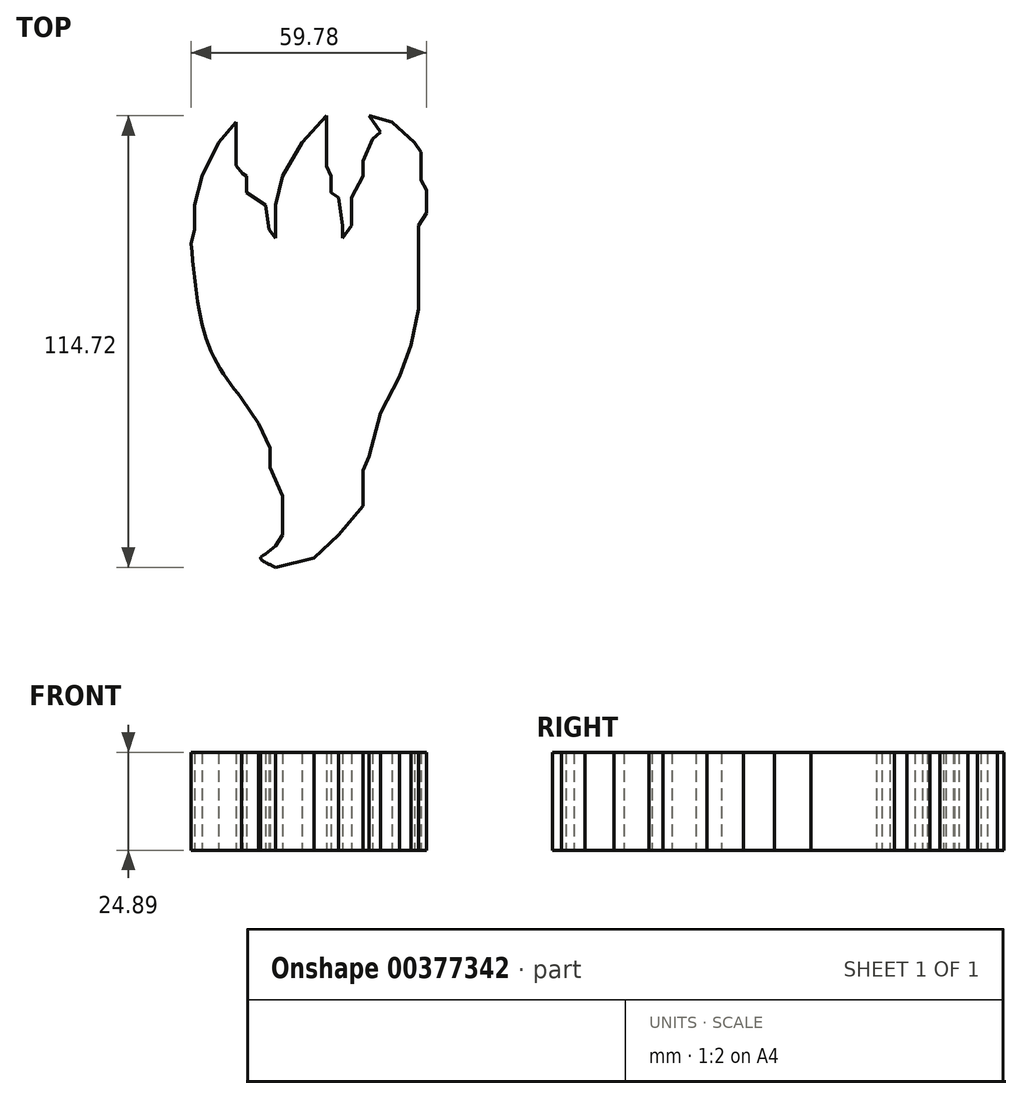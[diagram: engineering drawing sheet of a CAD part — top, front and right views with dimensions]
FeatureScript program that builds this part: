
annotation { "Feature Type Name" : "Feature", "Feature Type Description" : "" }
export const myFeature = defineFeature(function(context is Context, id is Id, definition is map)
    precondition{}
    {
        {
            var Q0;
            Q0=qCreatedBy(makeId("Top.planeOp"),FACE);
            var sketch = newSketch(context, id + "F0", { "sketchPlane" : qUnion([Q0])});
            skFitSpline(sketch, "E0", {"points": [v(-31.15, 30.49) * mm, v(-26.9, 4.93) * mm, v(-18.37, -8.92) * mm], "startDerivative": vector(4.39, -49.85) * mm, "endDerivative": vector(21.85, -28.13) * mm});
            skFitSpline(sketch, "E1", {"points": [v(-14.11, -15.3) * mm, v(-11.18, -21.43) * mm], "startDerivative": vector(2.93, -6.12) * mm, "endDerivative": vector(2.93, -6.12) * mm});
            skFitSpline(sketch, "E2", {"points": [v(-18.37, -8.92) * mm, v(-14.11, -15.3) * mm], "startDerivative": vector(4.26, -6.4) * mm, "endDerivative": vector(4.26, -6.4) * mm});
            skFitSpline(sketch, "E3", {"points": [v(-11.18, -21.43) * mm, v(-11.18, -26.5) * mm], "startDerivative": vector(0, -5.06) * mm, "endDerivative": vector(0, -5.06) * mm});
            skFitSpline(sketch, "E4", {"points": [v(-11.18, -26.5) * mm, v(-7.99, -33.68) * mm], "startDerivative": vector(3.2, -7.19) * mm, "endDerivative": vector(3.2, -7.19) * mm});
            skFitSpline(sketch, "E5", {"points": [v(-7.99, -33.68) * mm, v(-7.99, -37.52) * mm], "startDerivative": vector(0, -3.84) * mm, "endDerivative": vector(0, -3.84) * mm});
            skFitSpline(sketch, "E6", {"points": [v(-7.99, -36.24) * mm, v(-7.99, -43.6) * mm], "startDerivative": vector(0, -7.36) * mm, "endDerivative": vector(0, -7.36) * mm});
            skFitSpline(sketch, "E7", {"points": [v(-9.75, -46.33) * mm, v(-13.52, -49.47) * mm], "startDerivative": vector(-3.78, -3.15) * mm, "endDerivative": vector(-3.78, -3.15) * mm});
            skFitSpline(sketch, "E8", {"points": [v(-9.75, -46.33) * mm, v(-7.99, -43.6) * mm], "startDerivative": vector(1.76, 2.73) * mm, "endDerivative": vector(1.76, 2.73) * mm});
            skFitSpline(sketch, "E9", {"points": [v(-12.26, -48.42) * mm, v(-13.52, -49.47) * mm, v(-9.75, -51.78) * mm], "startDerivative": vector(-5.1, -2.6) * mm, "endDerivative": vector(9, -4) * mm});
            skFitSpline(sketch, "E10", {"points": [v(-9.75, -51.78) * mm, v(0, -49.47) * mm], "startDerivative": vector(9.75, 2.3) * mm, "endDerivative": vector(9.75, 2.3) * mm});
            skFitSpline(sketch, "E11", {"points": [v(0, -49.47) * mm, v(6.2, -43.6) * mm], "startDerivative": vector(6.2, 5.87) * mm, "endDerivative": vector(6.2, 5.87) * mm});
            skFitSpline(sketch, "E12", {"points": [v(6.2, -43.6) * mm, v(12.48, -36.24) * mm], "startDerivative": vector(6.3, 7.36) * mm, "endDerivative": vector(6.3, 7.36) * mm});
            skFitSpline(sketch, "E13", {"points": [v(12.48, -36.24) * mm, v(12.48, -27.24) * mm], "startDerivative": vector(0, 9) * mm, "endDerivative": vector(0, 9) * mm});
            skFitSpline(sketch, "E14", {"points": [v(12.48, -27.24) * mm, v(13.95, -23.68) * mm], "startDerivative": vector(1.47, 3.57) * mm, "endDerivative": vector(1.47, 3.57) * mm});
            skFitSpline(sketch, "E15", {"points": [v(13.95, -23.68) * mm, v(16.89, -12.56) * mm], "startDerivative": vector(2.94, 11.12) * mm, "endDerivative": vector(2.94, 11.12) * mm});
            skFitSpline(sketch, "E16", {"points": [v(16.89, -12.56) * mm, v(21.71, -3.33) * mm], "startDerivative": vector(4.82, 9.23) * mm, "endDerivative": vector(4.82, 9.23) * mm});
            skFitSpline(sketch, "E17", {"points": [v(21.71, -3.33) * mm, v(24.65, 4.64) * mm], "startDerivative": vector(2.94, 7.97) * mm, "endDerivative": vector(2.94, 7.97) * mm});
            skFitSpline(sketch, "E18", {"points": [v(24.65, 4.64) * mm, v(26.54, 13.87) * mm], "startDerivative": vector(1.89, 9.23) * mm, "endDerivative": vector(1.89, 9.23) * mm});
            skFitSpline(sketch, "E19", {"points": [v(26.54, 13.87) * mm, v(26.54, 22.47) * mm], "startDerivative": vector(0, 8.6) * mm, "endDerivative": vector(0, 8.6) * mm});
            skFitSpline(sketch, "E20", {"points": [v(26.54, 22.47) * mm, v(26.54, 30.23) * mm], "startDerivative": vector(0, 7.76) * mm, "endDerivative": vector(0, 7.76) * mm});
            skFitSpline(sketch, "E21", {"points": [v(26.54, 30.23) * mm, v(26.54, 35.05) * mm], "startDerivative": vector(0, 4.82) * mm, "endDerivative": vector(0, 4.82) * mm});
            skFitSpline(sketch, "E22", {"points": [v(26.54, 35.05) * mm, v(28.63, 38.2) * mm], "startDerivative": vector(2.1, 3.15) * mm, "endDerivative": vector(2.1, 3.15) * mm});
            skFitSpline(sketch, "E23", {"points": [v(28.63, 38.2) * mm, v(28.63, 44.07) * mm], "startDerivative": vector(0, 5.87) * mm, "endDerivative": vector(0, 5.87) * mm});
            skFitSpline(sketch, "E24", {"points": [v(28.63, 44.07) * mm, v(26.54, 47.84) * mm], "startDerivative": vector(-2.1, 3.78) * mm, "endDerivative": vector(-2.1, 3.78) * mm});
            skFitSpline(sketch, "E25", {"points": [v(27.23, 46.58) * mm, v(27.23, 53.72) * mm], "startDerivative": vector(0, 7.13) * mm, "endDerivative": vector(0, 7.13) * mm});
            skFitSpline(sketch, "E26", {"points": [v(27.23, 53.72) * mm, v(24.65, 57.28) * mm], "startDerivative": vector(-2.59, 3.57) * mm, "endDerivative": vector(-2.59, 3.57) * mm});
            skFitSpline(sketch, "E27", {"points": [v(25.51, 56.1) * mm, v(19.82, 61.27) * mm], "startDerivative": vector(-5.69, 5.17) * mm, "endDerivative": vector(-5.69, 5.17) * mm});
            skFitSpline(sketch, "E28", {"points": [v(19.82, 61.27) * mm, v(13.95, 62.94) * mm], "startDerivative": vector(-5.87, 1.68) * mm, "endDerivative": vector(-5.87, 1.68) * mm});
            skFitSpline(sketch, "E29", {"points": [v(13.95, 62.94) * mm, v(16.89, 58.75) * mm], "startDerivative": vector(2.94, -4.2) * mm, "endDerivative": vector(2.94, -4.2) * mm});
            skFitSpline(sketch, "E30", {"points": [v(16.89, 58.75) * mm, v(13.95, 56.1) * mm], "startDerivative": vector(-2.94, -2.66) * mm, "endDerivative": vector(-2.94, -2.66) * mm});
            skFitSpline(sketch, "E31", {"points": [v(14.93, 56.98) * mm, v(12.48, 51.4) * mm], "startDerivative": vector(-2.45, -5.57) * mm, "endDerivative": vector(-2.45, -5.57) * mm});
            skFitSpline(sketch, "E32", {"points": [v(12.48, 51.4) * mm, v(12.48, 48.47) * mm], "startDerivative": vector(0, -2.94) * mm, "endDerivative": vector(0, -2.94) * mm});
            skFitSpline(sketch, "E33", {"points": [v(12.48, 49.45) * mm, v(12.48, 46.58) * mm], "startDerivative": vector(0, -2.87) * mm, "endDerivative": vector(0, -2.87) * mm});
            skFitSpline(sketch, "E34", {"points": [v(12.48, 47.54) * mm, v(9.55, 42.18) * mm], "startDerivative": vector(-2.94, -5.36) * mm, "endDerivative": vector(-2.94, -5.36) * mm});
            skFitSpline(sketch, "E35", {"points": [v(9.55, 42.18) * mm, v(9.55, 35.05) * mm], "startDerivative": vector(0, -7.13) * mm, "endDerivative": vector(0, -7.13) * mm});
            skFitSpline(sketch, "E36", {"points": [v(9.55, 35.05) * mm, v(6.2, 30.23) * mm], "startDerivative": vector(-3.36, -4.82) * mm, "endDerivative": vector(-3.36, -4.82) * mm});
            skFitSpline(sketch, "E37", {"points": [v(7.31, 31.83) * mm, v(7.31, 35.05) * mm], "startDerivative": vector(0, 3.22) * mm, "endDerivative": vector(0, 3.22) * mm});
            skFitSpline(sketch, "E38", {"points": [v(7.31, 35.05) * mm, v(6.2, 42.18) * mm], "startDerivative": vector(-1.12, 7.13) * mm, "endDerivative": vector(-1.12, 7.13) * mm});
            skFitSpline(sketch, "E39", {"points": [v(6.2, 42.18) * mm, v(3.47, 44.07) * mm], "startDerivative": vector(-2.73, 1.89) * mm, "endDerivative": vector(-2.73, 1.89) * mm});
            skFitSpline(sketch, "E40", {"points": [v(4.37, 43.44) * mm, v(4.37, 47.54) * mm], "startDerivative": vector(0, 4.1) * mm, "endDerivative": vector(0, 4.1) * mm});
            skFitSpline(sketch, "E41", {"points": [v(4.37, 47.54) * mm, v(2.63, 51.4) * mm], "startDerivative": vector(-1.75, 3.87) * mm, "endDerivative": vector(-1.75, 3.87) * mm});
            skFitSpline(sketch, "E42", {"points": [v(3.2, 50.12) * mm, v(3.2, 53.72) * mm], "startDerivative": vector(0, 3.6) * mm, "endDerivative": vector(0, 3.6) * mm});
            skFitSpline(sketch, "E43", {"points": [v(3.2, 53.72) * mm, v(3.2, 62.94) * mm], "startDerivative": vector(0, 9.23) * mm, "endDerivative": vector(0, 9.23) * mm});
            skFitSpline(sketch, "E44", {"points": [v(3.2, 62.94) * mm, v(-3.04, 56.1) * mm], "startDerivative": vector(-6.25, -6.85) * mm, "endDerivative": vector(-6.25, -6.85) * mm});
            skFitSpline(sketch, "E45", {"points": [v(-3.04, 56.1) * mm, v(-7.99, 47.54) * mm], "startDerivative": vector(-4.95, -8.55) * mm, "endDerivative": vector(-4.95, -8.55) * mm});
            skFitSpline(sketch, "E46", {"points": [v(-7.99, 47.54) * mm, v(-9.75, 40.3) * mm], "startDerivative": vector(-1.76, -7.25) * mm, "endDerivative": vector(-1.76, -7.25) * mm});
            skFitSpline(sketch, "E47", {"points": [v(-9.75, 40.3) * mm, v(-9.75, 31.83) * mm], "startDerivative": vector(0, -8.46) * mm, "endDerivative": vector(0, -8.46) * mm});
            skFitSpline(sketch, "E48", {"points": [v(-9.75, 31.83) * mm, v(-12.26, 35.05) * mm], "startDerivative": vector(-2.52, 3.22) * mm, "endDerivative": vector(-2.52, 3.22) * mm});
            skFitSpline(sketch, "E49", {"points": [v(-11.43, 33.98) * mm, v(-12.26, 40.3) * mm], "startDerivative": vector(-0.84, 6.32) * mm, "endDerivative": vector(-0.84, 6.32) * mm});
            skFitSpline(sketch, "E50", {"points": [v(-12.26, 40.3) * mm, v(-17.09, 43.44) * mm], "startDerivative": vector(-4.82, 3.15) * mm, "endDerivative": vector(-4.82, 3.15) * mm});
            skFitSpline(sketch, "E51", {"points": [v(-17.09, 43.44) * mm, v(-17.09, 47.54) * mm], "startDerivative": vector(0, 4.1) * mm, "endDerivative": vector(0, 4.1) * mm});
            skFitSpline(sketch, "E52", {"points": [v(-17.09, 47.54) * mm, v(-20.02, 49.45) * mm], "startDerivative": vector(-2.94, 1.91) * mm, "endDerivative": vector(-2.94, 1.91) * mm});
            skFitSpline(sketch, "E53", {"points": [v(-18.07, 48.18) * mm, v(-20.65, 51.4) * mm], "startDerivative": vector(-2.59, 3.23) * mm, "endDerivative": vector(-2.59, 3.23) * mm});
            skFitSpline(sketch, "E54", {"points": [v(-19.8, 50.33) * mm, v(-19.8, 56.98) * mm], "startDerivative": vector(0, 6.65) * mm, "endDerivative": vector(0, 6.65) * mm});
            skFitSpline(sketch, "E55", {"points": [v(-19.8, 56.98) * mm, v(-19.8, 61.27) * mm], "startDerivative": vector(0, 4.29) * mm, "endDerivative": vector(0, 4.29) * mm});
            skFitSpline(sketch, "E56", {"points": [v(-19.8, 61.27) * mm, v(-24.22, 56.1) * mm], "startDerivative": vector(-4.43, -5.17) * mm, "endDerivative": vector(-4.43, -5.17) * mm});
            skFitSpline(sketch, "E57", {"points": [v(-24.22, 56.1) * mm, v(-28.41, 47.54) * mm], "startDerivative": vector(-4.2, -8.55) * mm, "endDerivative": vector(-4.2, -8.55) * mm});
            skFitSpline(sketch, "E58", {"points": [v(-28.41, 47.54) * mm, v(-30.3, 40.3) * mm], "startDerivative": vector(-1.89, -7.25) * mm, "endDerivative": vector(-1.89, -7.25) * mm});
            skFitSpline(sketch, "E59", {"points": [v(-30.3, 40.3) * mm, v(-30.3, 33.98) * mm], "startDerivative": vector(0, -6.32) * mm, "endDerivative": vector(0, -6.32) * mm});
            skFitSpline(sketch, "E60", {"points": [v(-30.3, 33.98) * mm, v(-31.15, 30.49) * mm], "startDerivative": vector(-0.85, -3.5) * mm, "endDerivative": vector(-0.85, -3.5) * mm});
            skSolve(sketch);
        }
        {
            var Q0;
            Q0 = qSketchRegion(id + "F0", true);
            extrude(context, id + "F1", {"entities" : qUnion([Q0]), "depth" : 24.9 * mm});
        }
    });
